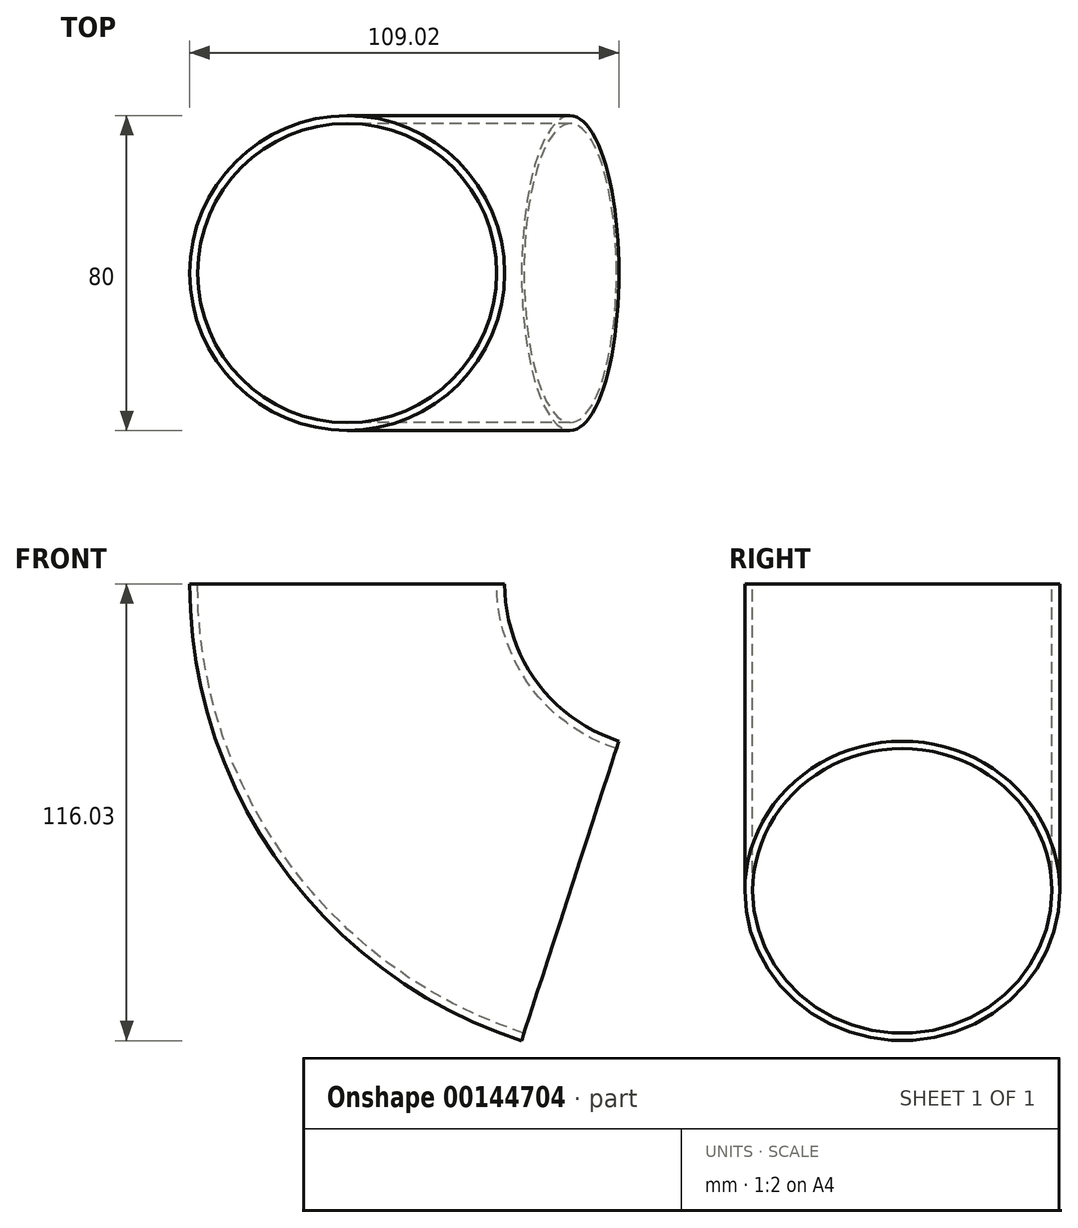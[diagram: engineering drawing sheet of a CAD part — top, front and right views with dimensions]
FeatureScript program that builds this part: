
annotation { "Feature Type Name" : "Feature", "Feature Type Description" : "" }
export const myFeature = defineFeature(function(context is Context, id is Id, definition is map)
    precondition{}
    {
        {
            assignVariable(context, id + "F0", {"name" : "kat", "anyValue" : 72});
        }
        {
            var Q0;
            Q0=qCreatedBy(makeId("Top.planeOp"),FACE);
            var sketch = newSketch(context, id + "F1", { "sketchPlane" : qUnion([Q0])});
            skCircle(sketch, "E0", {"center": v(-82, 0) * mm, "radius": 38 * mm});
            skCircle(sketch, "E1", {"center": v(-82, 0) * mm, "radius": 40 * mm});
            skLineSegment(sketch, "E2", {"start": v(0, 0) * mm, "end": v(0, -43.15) * mm});
            skSolve(sketch);
        }
        {
            var Q0;
            Q0=makeQuery(id+"F1.imprint","IMPRINT",FACE,{"disambiguationData":[TD([[makeQuery(id+"F1.imprint","IMPRINT",EDGE,{"derivedFrom":sQuery(id+"F1.wireOp",EDGE,"E0")}),-1.0]])]});
            var Q1;
            Q1=sQuery(id+"F1.wireOp",EDGE,"E2");
            revolve(context, id + "F2", {"entities" : qUnion([Q0]), "axis" : qUnion([Q1]), "revolveType" : RevolveType.ONE_DIRECTION, "angle" : (getVariable(context, 'kat')) * degree});
        }
    });
